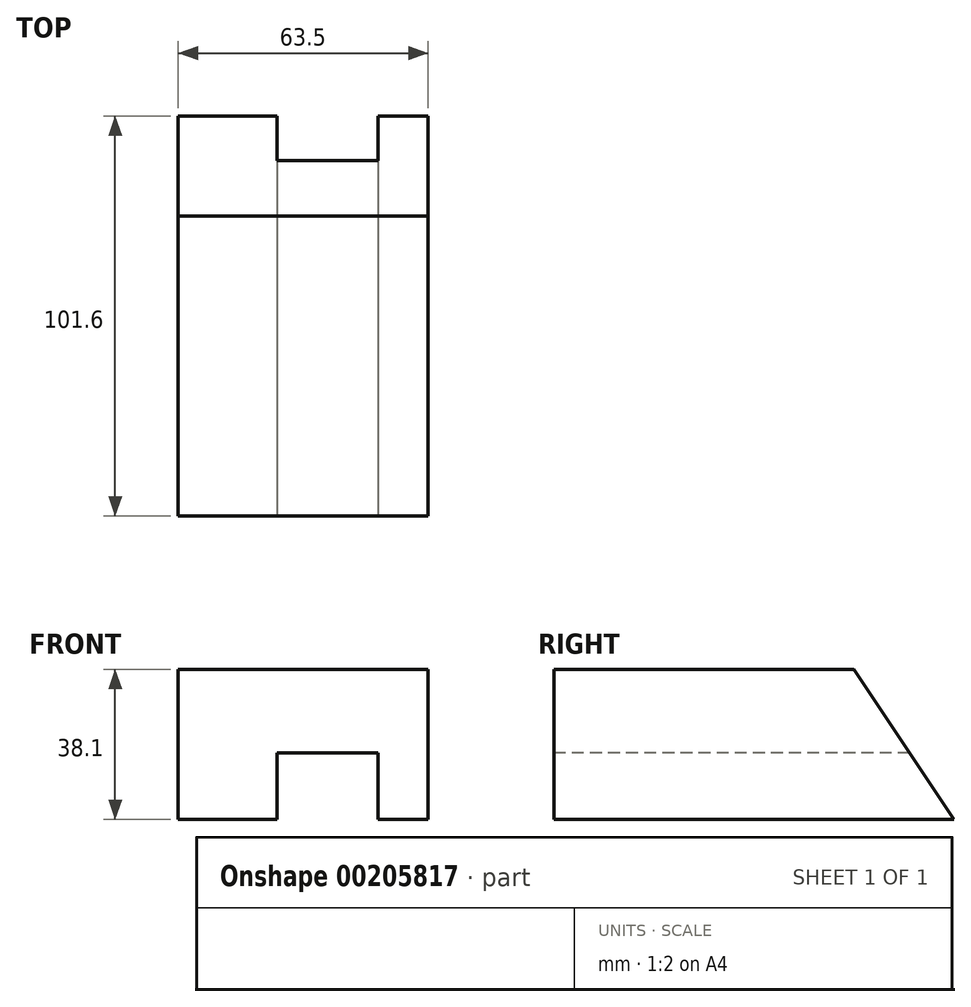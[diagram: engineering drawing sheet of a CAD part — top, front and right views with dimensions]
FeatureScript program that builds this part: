
annotation { "Feature Type Name" : "Feature", "Feature Type Description" : "" }
export const myFeature = defineFeature(function(context is Context, id is Id, definition is map)
    precondition{}
    {
        {
            var Q0;
            Q0=qCreatedBy(makeId("Right.planeOp"),FACE);
            var sketch = newSketch(context, id + "F0", { "sketchPlane" : qUnion([Q0])});
            skLineSegment(sketch, "E0.bottom", {"start": v(-50.8, 19.05) * mm, "end": v(25.4, 19.05) * mm});
            skLineSegment(sketch, "E0.top", {"start": v(-50.8, -19.05) * mm, "end": v(50.8, -19.05) * mm});
            skLineSegment(sketch, "E0.left", {"start": v(-50.8, 19.05) * mm, "end": v(-50.8, -19.05) * mm});
            skPoint(sketch, "E0.middle", {"position": v(0, 0) * mm});
            skLineSegment(sketch, "E1", {"start": v(50.8, -19.05) * mm, "end": v(25.4, 19.05) * mm});
            skSolve(sketch);
        }
        {
            var Q0;
            Q0=makeQuery(id+"F0.imprint","IMPRINT",FACE,{"disambiguationData":[TD([[makeQuery(id+"F0.imprint","IMPRINT",EDGE,{"derivedFrom":sQuery(id+"F0.wireOp",EDGE,"E0.bottom")}),-1.0]])]});
            extrude(context, id + "F1", {"entities" : qUnion([Q0]), "depth" : 63.5 * mm});
        }
        {
            var Q0;
            Q0=qCreatedBy(makeId("Front.planeOp"),FACE);
            var sketch = newSketch(context, id + "F2", { "sketchPlane" : qUnion([Q0])});
            skLineSegment(sketch, "E2.0.0", {"start": v(63.5, 19.05) * mm, "end": v(63.5, -19.05) * mm});
            skLineSegment(sketch, "E2.0.2", {"start": v(63.5, -19.05) * mm, "end": v(63.5, 19.05) * mm, "construction": true});
            skLineSegment(sketch, "E3.0.1", {"start": v(0, -19.05) * mm, "end": v(63.5, -19.05) * mm});
            skLineSegment(sketch, "E3.0.3", {"start": v(63.5, -19.05) * mm, "end": v(0, -19.05) * mm, "construction": true});
            skLineSegment(sketch, "E4.bottom", {"start": v(25.15, -19.05) * mm, "end": v(50.8, -19.05) * mm});
            skLineSegment(sketch, "E4.top", {"start": v(25.15, -2.13) * mm, "end": v(50.8, -2.13) * mm});
            skLineSegment(sketch, "E4.left", {"start": v(25.15, -19.05) * mm, "end": v(25.15, -2.13) * mm});
            skLineSegment(sketch, "E4.right", {"start": v(50.8, -19.05) * mm, "end": v(50.8, -2.13) * mm});
            skSolve(sketch);
        }
        {
            var Q0;
            Q0 = qSketchRegion(id + "F2", true);
            extrude(context, id + "F3", {"entities" : qUnion([Q0]), "operationType" : NewBodyOperationType.REMOVE, "endBound" : BoundingType.THROUGH_ALL, "oppositeDirection" : true, "depth" : 54.1 * mm, "hasSecondDirection" : true, "secondDirectionBound" : BoundingType.THROUGH_ALL, "secondDirectionOppositeDirection" : false, "secondDirectionDepth" : 25.4 * mm});
        }
    });
